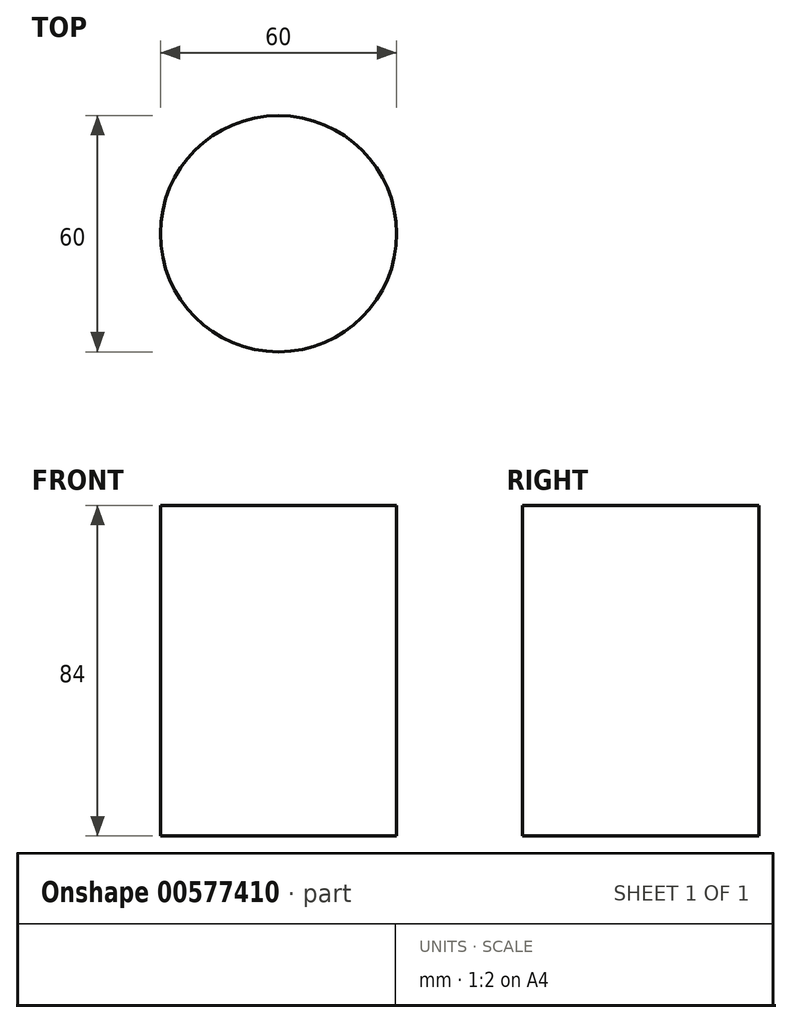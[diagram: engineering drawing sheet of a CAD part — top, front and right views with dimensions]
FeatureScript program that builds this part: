
annotation { "Feature Type Name" : "Feature", "Feature Type Description" : "" }
export const myFeature = defineFeature(function(context is Context, id is Id, definition is map)
    precondition{}
    {
        {
            var Q0;
            Q0=qCreatedBy(makeId("Top.planeOp"),FACE);
            var sketch = newSketch(context, id + "F0", { "sketchPlane" : qUnion([Q0])});
            skCircle(sketch, "E0", {"center": v(0, 0) * mm, "radius": 30 * mm});
            skSolve(sketch);
        }
        {
            var Q0;
            Q0 = qSketchRegion(id + "F0", true);
            extrude(context, id + "F1", {"entities" : qUnion([Q0]), "depth" : 84 * mm, "offsetDistance" : 25 * mm});
        }
    });
